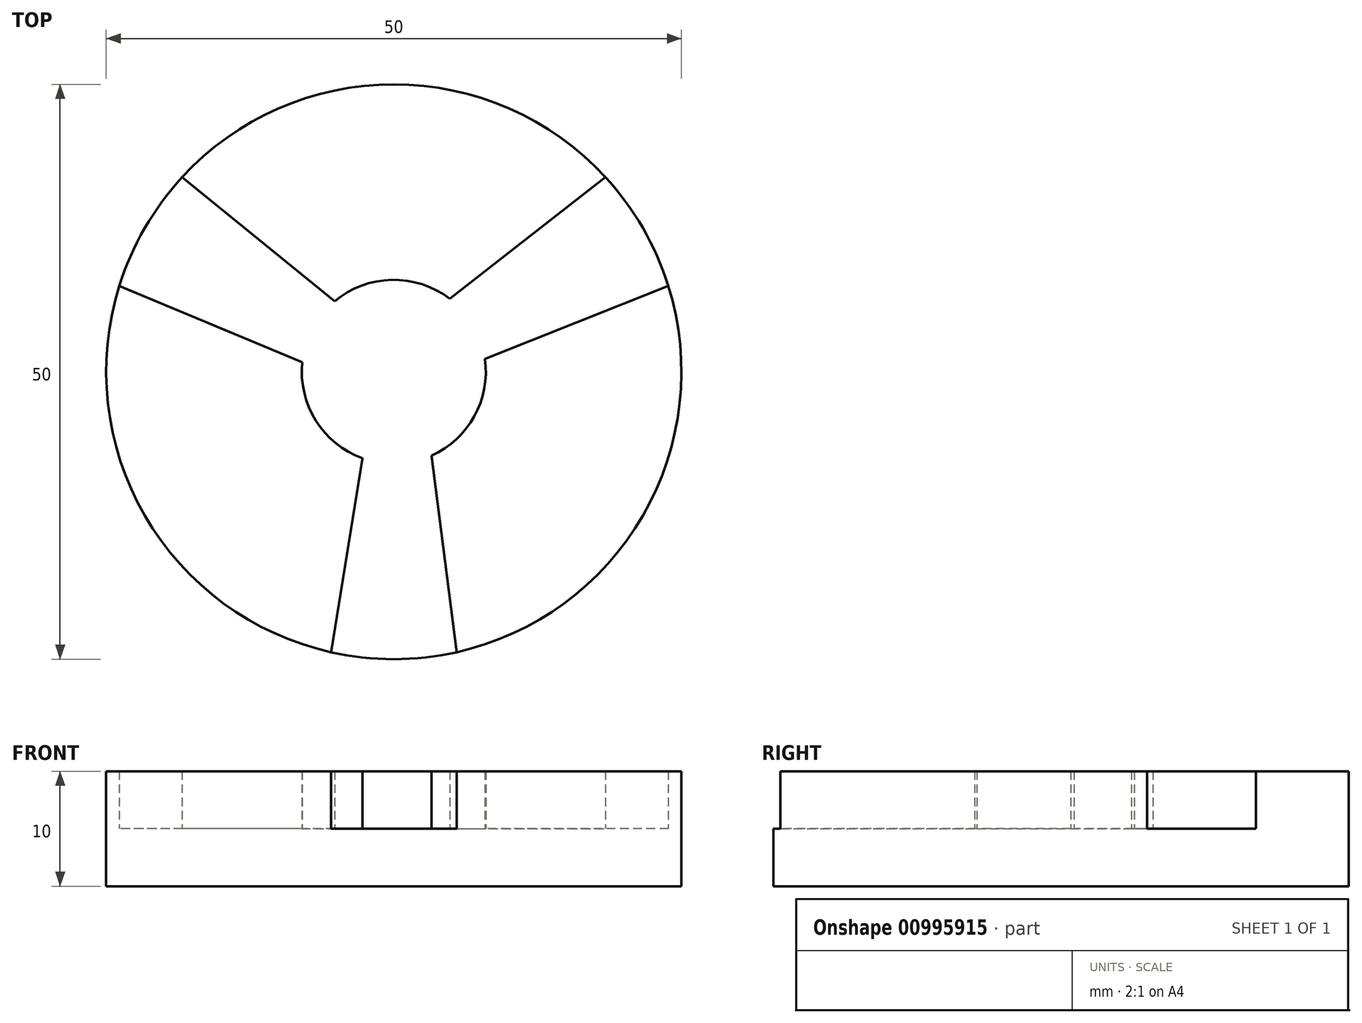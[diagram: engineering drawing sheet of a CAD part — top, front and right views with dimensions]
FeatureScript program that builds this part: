
annotation { "Feature Type Name" : "Feature", "Feature Type Description" : "" }
export const myFeature = defineFeature(function(context is Context, id is Id, definition is map)
    precondition{}
    {
        {
            var Q0;
            Q0=qCreatedBy(makeId("Top.planeOp"),FACE);
            var sketch = newSketch(context, id + "F0", { "sketchPlane" : qUnion([Q0])});
            skCircle(sketch, "E0", {"center": v(0, 0) * mm, "radius": 25 * mm});
            skSolve(sketch);
        }
        {
            var Q0;
            Q0 = qSketchRegion(id + "F0", true);
            extrude(context, id + "F1", {"entities" : qUnion([Q0]), "depth" : 5 * mm, "offsetDistance" : 25 * mm});
        }
        {
            var Q0;
            Q0=makeQuery(id+"F1.opExtrude","CAP_FACE",FACE,{"disambiguationData":[OSD([sQuery(id+"F0.wireOp",EDGE,"E0")])],"isStart":false});
            var sketch = newSketch(context, id + "F2", { "sketchPlane" : qUnion([Q0])});
            skCircle(sketch, "E1", {"center": v(0, 0) * mm, "radius": 8 * mm});
            skPoint(sketch, "E2", {"position": v(0, -8) * mm});
            skPoint(sketch, "E3", {"position": v(6.93, 4) * mm});
            skPoint(sketch, "E4", {"position": v(-6.93, 4) * mm});
            skPoint(sketch, "E5", {"position": v(-2.74, -7.52) * mm});
            skPoint(sketch, "E6", {"position": v(3.26, -7.3) * mm});
            skPoint(sketch, "E7", {"position": v(0, -25) * mm});
            skPoint(sketch, "E8", {"position": v(5.47, -24.4) * mm});
            skPoint(sketch, "E9", {"position": v(-5.47, -24.4) * mm});
            skLineSegment(sketch, "E10", {"start": v(3.26, -7.3) * mm, "end": v(5.47, -24.4) * mm});
            skLineSegment(sketch, "E11", {"start": v(-5.47, -24.4) * mm, "end": v(-2.74, -7.52) * mm});
            skLineSegment(sketch, "E12", {"start": v(-6.93, 4) * mm, "end": v(6.93, 4) * mm});
            skLineSegment(sketch, "E13", {"start": v(6.93, 4) * mm, "end": v(0, -8) * mm});
            skLineSegment(sketch, "E14", {"start": v(0, -8) * mm, "end": v(-6.93, 4) * mm});
            skPoint(sketch, "E15", {"position": v(4.86, 6.35) * mm});
            skPoint(sketch, "E16", {"position": v(7.37, 0.9) * mm});
            skPoint(sketch, "E17", {"position": v(-5.15, 6.13) * mm});
            skPoint(sketch, "E18", {"position": v(-7.96, 0.82) * mm});
            skPoint(sketch, "E19", {"position": v(21.65, 12.5) * mm});
            skPoint(sketch, "E20", {"position": v(-21.65, 12.5) * mm});
            skLineSegment(sketch, "E21", {"start": v(-21.65, 12.5) * mm, "end": v(21.65, 12.5) * mm});
            skLineSegment(sketch, "E22", {"start": v(21.65, 12.5) * mm, "end": v(0, -25) * mm});
            skLineSegment(sketch, "E23", {"start": v(0, -25) * mm, "end": v(-21.65, 12.5) * mm});
            skPoint(sketch, "E24", {"position": v(23.86, 7.46) * mm});
            skPoint(sketch, "E25", {"position": v(18.4, 16.93) * mm});
            skPoint(sketch, "E26", {"position": v(-18.4, 16.93) * mm});
            skPoint(sketch, "E27", {"position": v(-23.86, 7.46) * mm});
            skLineSegment(sketch, "E28", {"start": v(-7.96, 0.82) * mm, "end": v(-23.86, 7.46) * mm});
            skLineSegment(sketch, "E29", {"start": v(-5.15, 6.13) * mm, "end": v(-18.4, 16.93) * mm});
            skLineSegment(sketch, "E30", {"start": v(23.86, 7.46) * mm, "end": v(7.37, 0.9) * mm});
            skLineSegment(sketch, "E31", {"start": v(4.86, 6.35) * mm, "end": v(18.4, 16.93) * mm});
            skSolve(sketch);
        }
        {
            var Q0;
            {var subQ0=sQuery(id+"F2.wireOp",EDGE,"E29");var subQ1=sQuery(id+"F2.wireOp",EDGE,"E21");var subQ2=makeQuery(id+"F2.imprint","INTERSECT",VERTEX,{"derivedFrom":[subQ1,subQ0]});Q0=makeQuery(id+"F2.imprint","IMPRINT",FACE,{"disambiguationData":[TD([[makeQuery(id+"F2.imprint","IMPRINT",EDGE,{"disambiguationData":[TD([[subQ2,-1.0]])],"derivedFrom":subQ1}),1.0]])]});}
            var Q1;
            {var subQ0=sQuery(id+"F2.wireOp",EDGE,"E29");var subQ1=sQuery(id+"F2.wireOp",EDGE,"E1");var subQ2=makeQuery(id+"F2.imprint","INTERSECT",VERTEX,{"derivedFrom":[subQ1,subQ0]});Q1=makeQuery(id+"F2.imprint","IMPRINT",FACE,{"disambiguationData":[TD([[makeQuery(id+"F2.imprint","IMPRINT",EDGE,{"disambiguationData":[TD([[subQ2,1.0]])],"derivedFrom":subQ1}),-1.0]])]});}
            var Q2;
            {var subQ0=sQuery(id+"F2.wireOp",EDGE,"E10");var subQ1=sQuery(id+"F2.wireOp",EDGE,"E1");var subQ2=makeQuery(id+"F2.imprint","INTERSECT",VERTEX,{"derivedFrom":[subQ1,subQ0]});Q2=makeQuery(id+"F2.imprint","IMPRINT",FACE,{"disambiguationData":[TD([[makeQuery(id+"F2.imprint","IMPRINT",EDGE,{"disambiguationData":[TD([[subQ2,-1.0]])],"derivedFrom":subQ1}),-1.0]])]});}
            var Q3;
            {var subQ0=sQuery(id+"F2.wireOp",EDGE,"E10");var subQ1=makeQuery(id+"F1.opExtrude","CAP_EDGE",EDGE,{"disambiguationData":[OSD([sQuery(id+"F0.wireOp",EDGE,"E0")])],"isStart":false});var subQ2=makeQuery(id+"F2.imprint","INTERSECT",VERTEX,{"derivedFrom":[subQ1,subQ0]});Q3=makeQuery(id+"F2.imprint","IMPRINT",FACE,{"disambiguationData":[TD([[makeQuery(id+"F2.imprint","IMPRINT",EDGE,{"disambiguationData":[TD([[subQ2,1.0]])],"derivedFrom":subQ0}),1.0]])]});}
            var Q4;
            {var subQ0=sQuery(id+"F2.wireOp",EDGE,"E11");var subQ1=sQuery(id+"F2.wireOp",EDGE,"E1");var subQ2=makeQuery(id+"F2.imprint","INTERSECT",VERTEX,{"derivedFrom":[subQ1,subQ0]});Q4=makeQuery(id+"F2.imprint","IMPRINT",FACE,{"disambiguationData":[TD([[makeQuery(id+"F2.imprint","IMPRINT",EDGE,{"disambiguationData":[TD([[subQ2,1.0]])],"derivedFrom":subQ1}),-1.0]])]});}
            var Q5;
            {var subQ0=sQuery(id+"F2.wireOp",EDGE,"E11");var subQ1=makeQuery(id+"F1.opExtrude","CAP_EDGE",EDGE,{"disambiguationData":[OSD([sQuery(id+"F0.wireOp",EDGE,"E0")])],"isStart":false});var subQ2=makeQuery(id+"F2.imprint","INTERSECT",VERTEX,{"derivedFrom":[subQ1,subQ0]});Q5=makeQuery(id+"F2.imprint","IMPRINT",FACE,{"disambiguationData":[TD([[makeQuery(id+"F2.imprint","IMPRINT",EDGE,{"disambiguationData":[TD([[subQ2,-1.0]])],"derivedFrom":subQ0}),1.0]])]});}
            extrude(context, id + "F3", {"entities" : qUnion([Q0, Q1, Q2, Q3, Q4, Q5]), "operationType" : NewBodyOperationType.ADD, "depth" : 5 * mm, "offsetDistance" : 25 * mm});
        }
    });
